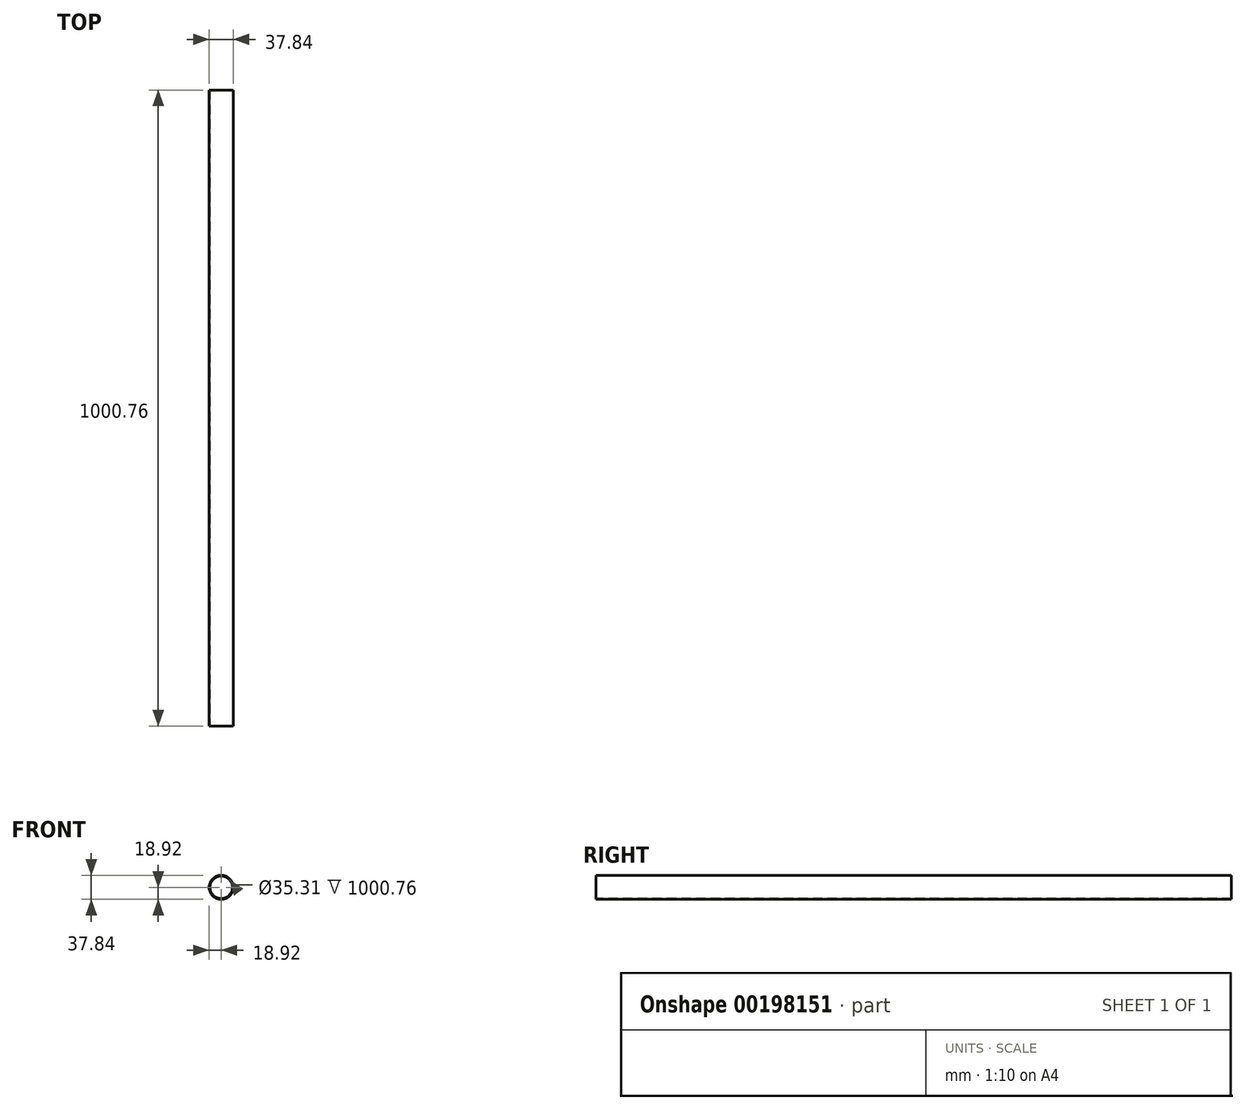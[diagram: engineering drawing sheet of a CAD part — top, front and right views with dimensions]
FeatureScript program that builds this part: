
annotation { "Feature Type Name" : "Feature", "Feature Type Description" : "" }
export const myFeature = defineFeature(function(context is Context, id is Id, definition is map)
    precondition{}
    {
        {
            var Q0;
            Q0=qCreatedBy(makeId("Front.planeOp"),FACE);
            var sketch = newSketch(context, id + "F0", { "sketchPlane" : qUnion([Q0])});
            skCircle(sketch, "E0", {"center": v(0, 0) * mm, "radius": 18.92 * mm});
            skCircle(sketch, "E1", {"center": v(0, 0) * mm, "radius": 17.65 * mm});
            skSolve(sketch);
        }
        {
            var Q0;
            Q0 = qSketchRegion(id + "F0", true);
            extrude(context, id + "F1", {"entities" : qUnion([Q0]), "oppositeDirection" : true, "depth" : 1000.76 * mm});
        }
    });
